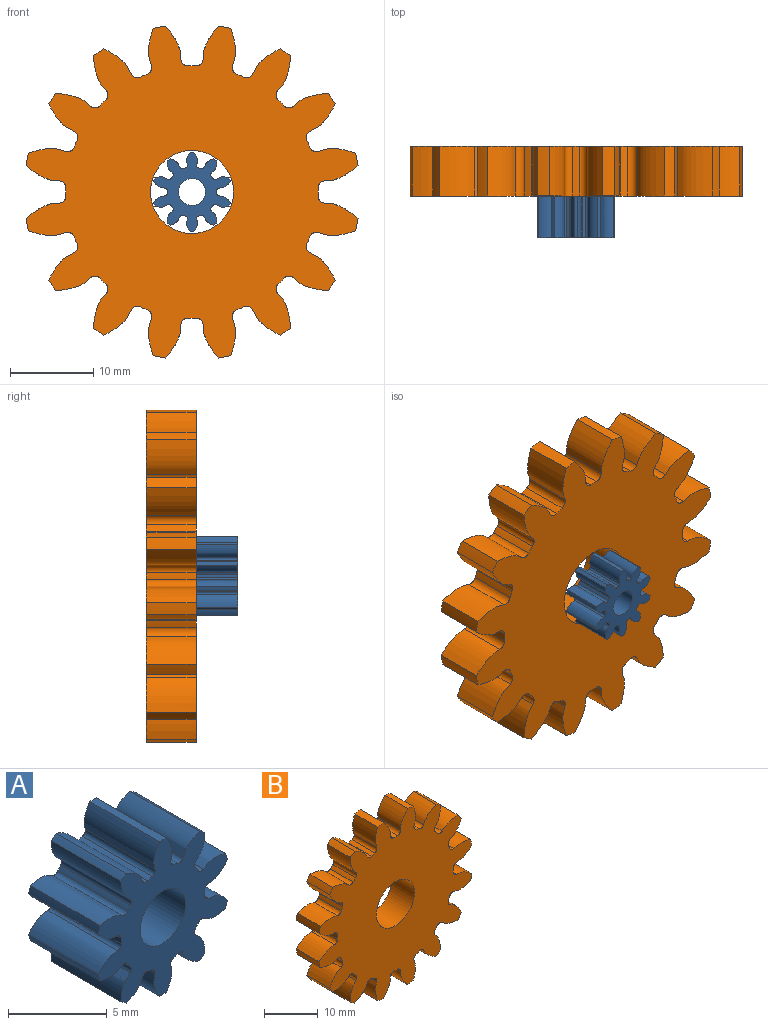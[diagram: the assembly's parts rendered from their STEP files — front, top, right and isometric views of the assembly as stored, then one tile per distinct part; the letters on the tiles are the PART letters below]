
ASSEMBLY  parts=2 mates=1
PART A: 63 faces, bbox 9.3x5x9.6 mm
  f0: extruded ~5x1.39mm, area 8.3mm2, adj f40,f41,f42,f43
  f1: cylinder r=3mm len=5mm, axis (0,1,0), area 1.7mm2, adj f41,f42,f43,f44
  f2: extruded ~5x1.39mm, area 8.3mm2, adj f3,f41,f42,f44
  f3: cylinder r=4.8mm len=5mm, axis (0,1,0), area 2.3mm2, adj f2,f4,f41,f42
  f4: extruded ~5x1.59mm, area 8.3mm2, adj f3,f41,f42,f45
  f5: cylinder r=3mm len=5mm, axis (0,1,0), area 1.7mm2, adj f41,f42,f45,f46
  f6: extruded ~5x1.46mm, area 8.3mm2, adj f7,f41,f42,f46
  f7: cylinder r=4.8mm len=5mm, axis (0,1,0), area 2.3mm2, adj f6,f8,f41,f42
  f8: extruded ~5x1.19mm, area 8.3mm2, adj f7,f41,f42,f47
  f9: cylinder r=3mm len=5mm, axis (0,1,0), area 1.7mm2, adj f41,f42,f47,f48
  f10: extruded ~5x1.57mm, area 8.3mm2, adj f11,f41,f42,f48
  f11: cylinder r=4.8mm len=5mm, axis (0,1,0), area 2.3mm2, adj f10,f12,f41,f42
  f12: extruded ~5x1.57mm, area 8.3mm2, adj f11,f41,f42,f49
  f13: cylinder r=3mm len=5mm, axis (0,1,0), area 1.7mm2, adj f41,f42,f49,f50
  f14: extruded ~5x1.19mm, area 8.3mm2, adj f15,f41,f42,f50
  f15: cylinder r=4.8mm len=5mm, axis (0,1,0), area 2.3mm2, adj f14,f16,f41,f42
  f16: extruded ~5x1.46mm, area 8.3mm2, adj f15,f41,f42,f51
  f17: cylinder r=3mm len=5mm, axis (0,1,0), area 1.7mm2, adj f41,f42,f51,f52
  f18: extruded ~5x1.59mm, area 8.3mm2, adj f19,f41,f42,f52
  f19: cylinder r=4.8mm len=5mm, axis (0,1,0), area 2.3mm2, adj f18,f20,f41,f42
  f20: extruded ~5x1.39mm, area 8.3mm2, adj f19,f41,f42,f53
  f21: cylinder r=3mm len=5mm, axis (0,1,0), area 1.7mm2, adj f41,f42,f53,f54
  f22: extruded ~5x1.39mm, area 8.3mm2, adj f23,f41,f42,f54
  f23: cylinder r=4.8mm len=5mm, axis (0,1,0), area 2.3mm2, adj f22,f24,f41,f42
  f24: extruded ~5x1.59mm, area 8.3mm2, adj f23,f41,f42,f55
  f25: cylinder r=3mm len=5mm, axis (0,1,0), area 1.7mm2, adj f41,f42,f55,f56
  f26: extruded ~5x1.46mm, area 8.3mm2, adj f27,f41,f42,f56
  f27: cylinder r=4.8mm len=5mm, axis (0,1,0), area 2.3mm2, adj f26,f28,f41,f42
  f28: extruded ~5x1.19mm, area 8.3mm2, adj f27,f41,f42,f57
  f29: cylinder r=3mm len=5mm, axis (0,1,0), area 1.7mm2, adj f41,f42,f57,f58
  f30: extruded ~5x1.57mm, area 8.3mm2, adj f31,f41,f42,f58
  f31: cylinder r=4.8mm len=5mm, axis (0,1,0), area 2.3mm2, adj f30,f32,f41,f42
  f32: extruded ~5x1.57mm, area 8.3mm2, adj f31,f41,f42,f59
  f33: cylinder r=3mm len=5mm, axis (0,1,0), area 1.7mm2, adj f41,f42,f59,f60
  f34: extruded ~5x1.19mm, area 8.3mm2, adj f35,f41,f42,f60
  f35: cylinder r=4.8mm len=5mm, axis (0,1,0), area 2.3mm2, adj f34,f36,f41,f42
  f36: extruded ~5x1.46mm, area 8.3mm2, adj f35,f41,f42,f61
  f37: cylinder r=3mm len=5mm, axis (0,1,0), area 1.7mm2, adj f41,f42,f61,f62
  f38: extruded ~5x1.59mm, area 8.3mm2, adj f40,f41,f42,f62
  f39: cylinder r=1.62mm len=5mm, axis (0,1,0), area 51.1mm2, adj f41,f42
  f40: cylinder r=4.8mm len=5mm, axis (0,1,0), area 2.3mm2, adj f0,f38,f41,f42
  f41: plane 9.62x9.29mm, normal (0,-1,0), area 39.7mm2, adj f0,f1,f2,f3,f4,f5,f6,f7
  f42: plane 9.62x9.29mm, normal (0,1,0), area 39.7mm2, adj f0,f1,f2,f3,f4,f5,f6,f7
  f43: cylinder r=0.28mm len=5mm, axis (0,1,0), area 2.1mm2, adj f0,f1,f41,f42
  f44: cylinder r=0.28mm len=5mm, axis (0,1,0), area 2.1mm2, adj f1,f2,f41,f42
  f45: cylinder r=0.28mm len=5mm, axis (0,1,0), area 2.1mm2, adj f4,f5,f41,f42
  f46: cylinder r=0.28mm len=5mm, axis (0,1,0), area 2.1mm2, adj f5,f6,f41,f42
  f47: cylinder r=0.28mm len=5mm, axis (0,1,0), area 2.1mm2, adj f8,f9,f41,f42
  f48: cylinder r=0.28mm len=5mm, axis (0,1,0), area 2.1mm2, adj f9,f10,f41,f42
  f49: cylinder r=0.28mm len=5mm, axis (0,1,0), area 2.1mm2, adj f12,f13,f41,f42
  f50: cylinder r=0.28mm len=5mm, axis (0,1,0), area 2.1mm2, adj f13,f14,f41,f42
  f51: cylinder r=0.28mm len=5mm, axis (0,1,0), area 2.1mm2, adj f16,f17,f41,f42
  f52: cylinder r=0.28mm len=5mm, axis (0,1,0), area 2.1mm2, adj f17,f18,f41,f42
  f53: cylinder r=0.28mm len=5mm, axis (0,1,0), area 2.1mm2, adj f20,f21,f41,f42
  f54: cylinder r=0.28mm len=5mm, axis (0,1,0), area 2.1mm2, adj f21,f22,f41,f42
  f55: cylinder r=0.28mm len=5mm, axis (0,1,0), area 2.1mm2, adj f24,f25,f41,f42
  f56: cylinder r=0.28mm len=5mm, axis (0,1,0), area 2.1mm2, adj f25,f26,f41,f42
  f57: cylinder r=0.28mm len=5mm, axis (0,1,0), area 2.1mm2, adj f28,f29,f41,f42
  f58: cylinder r=0.28mm len=5mm, axis (0,1,0), area 2.1mm2, adj f29,f30,f41,f42
  f59: cylinder r=0.28mm len=5mm, axis (0,1,0), area 2.1mm2, adj f32,f33,f41,f42
  f60: cylinder r=0.28mm len=5mm, axis (0,1,0), area 2.1mm2, adj f33,f34,f41,f42
  f61: cylinder r=0.28mm len=5mm, axis (0,1,0), area 2.1mm2, adj f36,f37,f41,f42
  f62: cylinder r=0.28mm len=5mm, axis (0,1,0), area 2.1mm2, adj f37,f38,f41,f42
PART B: 99 faces, bbox 40x6x40 mm
  f0: extruded ~6x4.04mm, area 27.4mm2, adj f64,f65,f66,f67
  f1: cylinder r=15.19mm len=6mm, axis (0,1,0), area 5.6mm2, adj f65,f66,f67,f68
  f2: extruded ~6x4.04mm, area 27.4mm2, adj f3,f65,f66,f68
  f3: cylinder r=20.25mm len=6mm, axis (0,1,0), area 9mm2, adj f2,f4,f65,f66
  f4: extruded ~6x4.45mm, area 27.4mm2, adj f3,f65,f66,f69
  f5: cylinder r=15.19mm len=6mm, axis (0,1,0), area 5.6mm2, adj f65,f66,f69,f70
  f6: extruded ~6x3.29mm, area 27.4mm2, adj f7,f65,f66,f70
  f7: cylinder r=20.25mm len=6mm, axis (0,1,0), area 9mm2, adj f6,f8,f65,f66
  f8: extruded ~6x4.19mm, area 27.4mm2, adj f7,f65,f66,f71
  f9: cylinder r=15.19mm len=6mm, axis (0,1,0), area 5.6mm2, adj f65,f66,f71,f72
  f10: extruded ~6x4.19mm, area 27.4mm2, adj f11,f65,f66,f72
  f11: cylinder r=20.25mm len=6mm, axis (0,1,0), area 9mm2, adj f10,f12,f65,f66
  f12: extruded ~6x3.29mm, area 27.4mm2, adj f11,f65,f66,f73
  f13: cylinder r=15.19mm len=6mm, axis (0,1,0), area 5.6mm2, adj f65,f66,f73,f74
  f14: extruded ~6x4.45mm, area 27.4mm2, adj f15,f65,f66,f74
  f15: cylinder r=20.25mm len=6mm, axis (0,1,0), area 9mm2, adj f14,f16,f65,f66
  f16: extruded ~6x4.04mm, area 27.4mm2, adj f15,f65,f66,f75
  f17: cylinder r=15.19mm len=6mm, axis (0,1,0), area 5.6mm2, adj f65,f66,f75,f76
  f18: extruded ~6x4.04mm, area 27.4mm2, adj f19,f65,f66,f76
  f19: cylinder r=20.25mm len=6mm, axis (0,1,0), area 9mm2, adj f18,f20,f65,f66
  f20: extruded ~6x4.45mm, area 27.4mm2, adj f19,f65,f66,f77
  f21: cylinder r=15.19mm len=6mm, axis (0,1,0), area 5.6mm2, adj f65,f66,f77,f78
  f22: extruded ~6x3.29mm, area 27.4mm2, adj f23,f65,f66,f78
  f23: cylinder r=20.25mm len=6mm, axis (0,1,0), area 9mm2, adj f22,f24,f65,f66
  f24: extruded ~6x4.19mm, area 27.4mm2, adj f23,f65,f66,f79
  f25: cylinder r=15.19mm len=6mm, axis (0,1,0), area 5.6mm2, adj f65,f66,f79,f80
  f26: extruded ~6x4.19mm, area 27.4mm2, adj f27,f65,f66,f80
  f27: cylinder r=20.25mm len=6mm, axis (0,1,0), area 9mm2, adj f26,f28,f65,f66
  f28: extruded ~6x3.29mm, area 27.4mm2, adj f27,f65,f66,f81
  f29: cylinder r=15.19mm len=6mm, axis (0,1,0), area 5.6mm2, adj f65,f66,f81,f82
  f30: extruded ~6x4.45mm, area 27.4mm2, adj f31,f65,f66,f82
  f31: cylinder r=20.25mm len=6mm, axis (0,1,0), area 9mm2, adj f30,f32,f65,f66
  f32: extruded ~6x4.04mm, area 27.4mm2, adj f31,f65,f66,f83
  f33: cylinder r=15.19mm len=6mm, axis (0,1,0), area 5.6mm2, adj f65,f66,f83,f84
  f34: extruded ~6x4.04mm, area 27.4mm2, adj f35,f65,f66,f84
  f35: cylinder r=20.25mm len=6mm, axis (0,1,0), area 9mm2, adj f34,f36,f65,f66
  f36: extruded ~6x4.45mm, area 27.4mm2, adj f35,f65,f66,f85
  f37: cylinder r=15.19mm len=6mm, axis (0,1,0), area 5.6mm2, adj f65,f66,f85,f86
  f38: extruded ~6x3.29mm, area 27.4mm2, adj f39,f65,f66,f86
  f39: cylinder r=20.25mm len=6mm, axis (0,1,0), area 9mm2, adj f38,f40,f65,f66
  f40: extruded ~6x4.19mm, area 27.4mm2, adj f39,f65,f66,f87
  f41: cylinder r=15.19mm len=6mm, axis (0,1,0), area 5.6mm2, adj f65,f66,f87,f88
  f42: extruded ~6x4.19mm, area 27.4mm2, adj f43,f65,f66,f88
  f43: cylinder r=20.25mm len=6mm, axis (0,1,0), area 9mm2, adj f42,f44,f65,f66
  f44: extruded ~6x3.29mm, area 27.4mm2, adj f43,f65,f66,f89
  f45: cylinder r=15.19mm len=6mm, axis (0,1,0), area 5.6mm2, adj f65,f66,f89,f90
  f46: extruded ~6x4.45mm, area 27.4mm2, adj f47,f65,f66,f90
  f47: cylinder r=20.25mm len=6mm, axis (0,1,0), area 9mm2, adj f46,f48,f65,f66
  f48: extruded ~6x4.04mm, area 27.4mm2, adj f47,f65,f66,f91
  f49: cylinder r=15.19mm len=6mm, axis (0,1,0), area 5.6mm2, adj f65,f66,f91,f92
  f50: extruded ~6x4.04mm, area 27.4mm2, adj f51,f65,f66,f92
  f51: cylinder r=20.25mm len=6mm, axis (0,1,0), area 9mm2, adj f50,f52,f65,f66
  f52: extruded ~6x4.45mm, area 27.4mm2, adj f51,f65,f66,f93
  f53: cylinder r=15.19mm len=6mm, axis (0,1,0), area 5.6mm2, adj f65,f66,f93,f94
  f54: extruded ~6x3.29mm, area 27.4mm2, adj f55,f65,f66,f94
  f55: cylinder r=20.25mm len=6mm, axis (0,1,0), area 9mm2, adj f54,f56,f65,f66
  f56: extruded ~6x4.19mm, area 27.4mm2, adj f55,f65,f66,f95
  f57: cylinder r=15.19mm len=6mm, axis (0,1,0), area 5.6mm2, adj f65,f66,f95,f96
  f58: extruded ~6x4.19mm, area 27.4mm2, adj f59,f65,f66,f96
  f59: cylinder r=20.25mm len=6mm, axis (0,1,0), area 9mm2, adj f58,f60,f65,f66
  f60: extruded ~6x3.29mm, area 27.4mm2, adj f59,f65,f66,f97
  f61: cylinder r=15.19mm len=6mm, axis (0,1,0), area 5.6mm2, adj f65,f66,f97,f98
  f62: extruded ~6x4.45mm, area 27.4mm2, adj f64,f65,f66,f98
  f63: cylinder r=5mm len=10mm, axis (0,1,0), area 188.5mm2, adj f65,f66
  f64: cylinder r=20.25mm len=6mm, axis (0,1,0), area 9mm2, adj f0,f62,f65,f66
  f65: plane 40.04x40.04mm, normal (0,-1,0), area 911.2mm2, adj f0,f1,f2,f3,f4,f5,f6,f7
  f66: plane 40.04x40.04mm, normal (0,1,0), area 911.2mm2, adj f0,f1,f2,f3,f4,f5,f6,f7
  f67: cylinder r=0.84mm len=6mm, axis (0,1,0), area 7.7mm2, adj f0,f1,f65,f66
  f68: cylinder r=0.84mm len=6mm, axis (0,1,0), area 7.7mm2, adj f1,f2,f65,f66
  f69: cylinder r=0.84mm len=6mm, axis (0,1,0), area 7.7mm2, adj f4,f5,f65,f66
  f70: cylinder r=0.84mm len=6mm, axis (0,1,0), area 7.7mm2, adj f5,f6,f65,f66
  f71: cylinder r=0.84mm len=6mm, axis (0,1,0), area 7.7mm2, adj f8,f9,f65,f66
  f72: cylinder r=0.84mm len=6mm, axis (0,1,0), area 7.7mm2, adj f9,f10,f65,f66
  f73: cylinder r=0.84mm len=6mm, axis (0,1,0), area 7.7mm2, adj f12,f13,f65,f66
  f74: cylinder r=0.84mm len=6mm, axis (0,1,0), area 7.7mm2, adj f13,f14,f65,f66
  f75: cylinder r=0.84mm len=6mm, axis (0,1,0), area 7.7mm2, adj f16,f17,f65,f66
  f76: cylinder r=0.84mm len=6mm, axis (0,1,0), area 7.7mm2, adj f17,f18,f65,f66
  f77: cylinder r=0.84mm len=6mm, axis (0,1,0), area 7.7mm2, adj f20,f21,f65,f66
  f78: cylinder r=0.84mm len=6mm, axis (0,1,0), area 7.7mm2, adj f21,f22,f65,f66
  f79: cylinder r=0.84mm len=6mm, axis (0,1,0), area 7.7mm2, adj f24,f25,f65,f66
  f80: cylinder r=0.84mm len=6mm, axis (0,1,0), area 7.7mm2, adj f25,f26,f65,f66
  f81: cylinder r=0.84mm len=6mm, axis (0,1,0), area 7.7mm2, adj f28,f29,f65,f66
  f82: cylinder r=0.84mm len=6mm, axis (0,1,0), area 7.7mm2, adj f29,f30,f65,f66
  f83: cylinder r=0.84mm len=6mm, axis (0,1,0), area 7.7mm2, adj f32,f33,f65,f66
  f84: cylinder r=0.84mm len=6mm, axis (0,1,0), area 7.7mm2, adj f33,f34,f65,f66
  f85: cylinder r=0.84mm len=6mm, axis (0,1,0), area 7.7mm2, adj f36,f37,f65,f66
  f86: cylinder r=0.84mm len=6mm, axis (0,1,0), area 7.7mm2, adj f37,f38,f65,f66
  f87: cylinder r=0.84mm len=6mm, axis (0,1,0), area 7.7mm2, adj f40,f41,f65,f66
  f88: cylinder r=0.84mm len=6mm, axis (0,1,0), area 7.7mm2, adj f41,f42,f65,f66
  f89: cylinder r=0.84mm len=6mm, axis (0,1,0), area 7.7mm2, adj f44,f45,f65,f66
  f90: cylinder r=0.84mm len=6mm, axis (0,1,0), area 7.7mm2, adj f45,f46,f65,f66
  f91: cylinder r=0.84mm len=6mm, axis (0,1,0), area 7.7mm2, adj f48,f49,f65,f66
  f92: cylinder r=0.84mm len=6mm, axis (0,1,0), area 7.7mm2, adj f49,f50,f65,f66
  f93: cylinder r=0.84mm len=6mm, axis (0,1,0), area 7.7mm2, adj f52,f53,f65,f66
  f94: cylinder r=0.84mm len=6mm, axis (0,1,0), area 7.7mm2, adj f53,f54,f65,f66
  f95: cylinder r=0.84mm len=6mm, axis (0,1,0), area 7.7mm2, adj f56,f57,f65,f66
  f96: cylinder r=0.84mm len=6mm, axis (0,1,0), area 7.7mm2, adj f57,f58,f65,f66
  f97: cylinder r=0.84mm len=6mm, axis (0,1,0), area 7.7mm2, adj f60,f61,f65,f66
  f98: cylinder r=0.84mm len=6mm, axis (0,1,0), area 7.7mm2, adj f61,f62,f65,f66
PLACE A t=(-2.46,19.22,23.39)mm
PLACE B t=(-2.46,25.22,23.39)mm
MATE fastened B.f13 <-> A.f29  axis (0,-1,0) through (-2.46,19.22,23.39)mm
